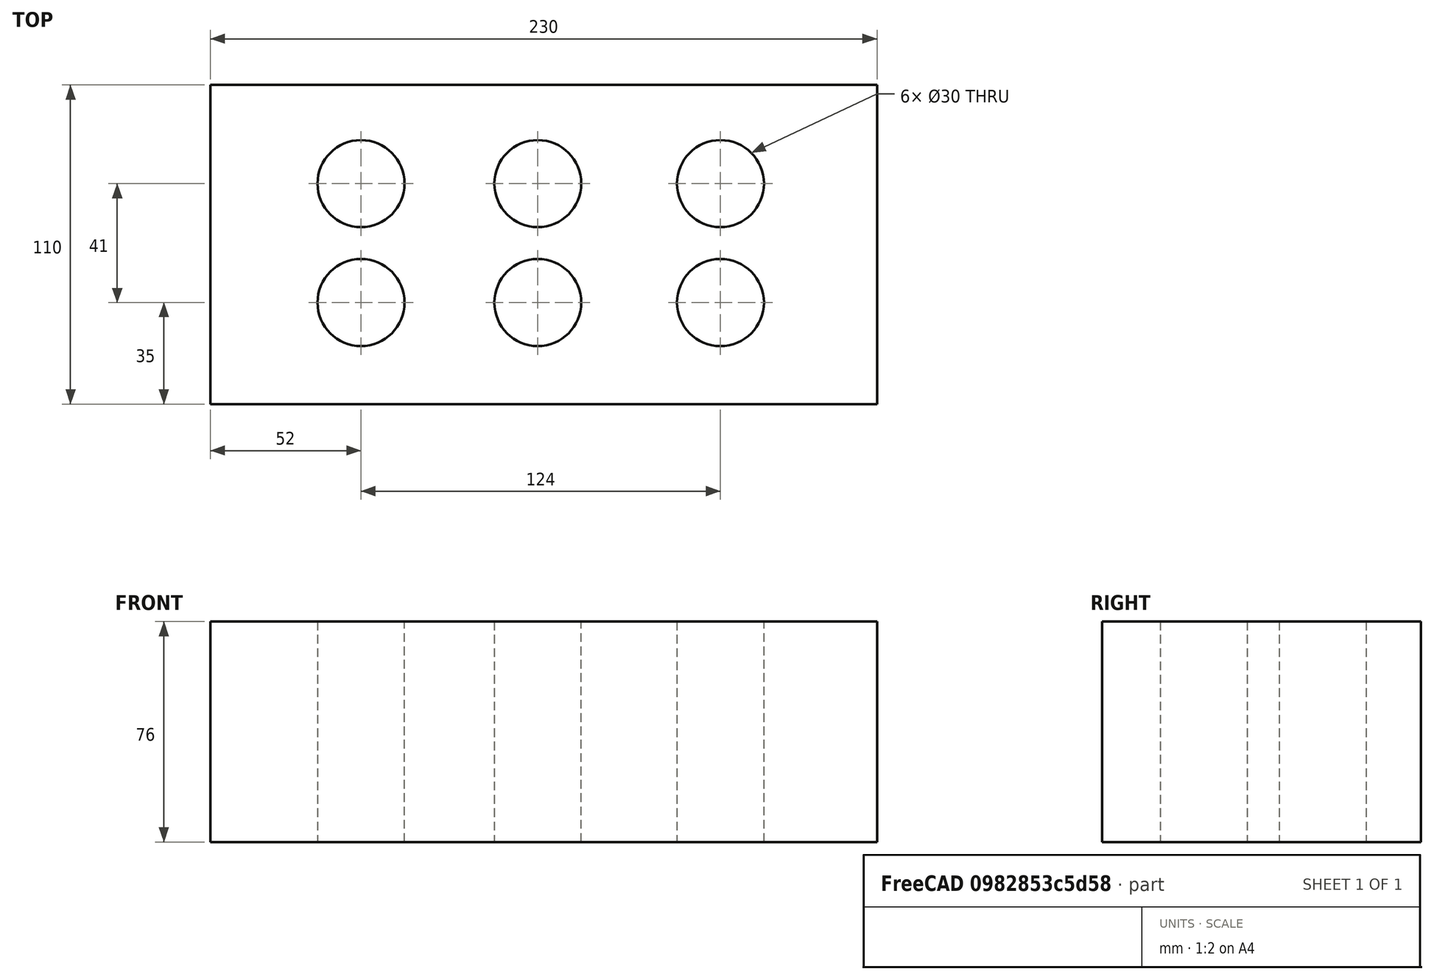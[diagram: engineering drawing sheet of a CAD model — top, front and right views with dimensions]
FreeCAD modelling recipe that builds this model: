
FCSTD DOCUMENT  (FreeCAD 1.0R39319 (Git))
Label: ojt1_t09r02_brik
License: All rights reserved
LicenseURL: https://en.wikipedia.org/wiki/All_rights_reserved
objects: Part::Cylinder×6, Part::Cut×6, Part::Box×1
note: 13 computed .brp shape members not serialized (recipe doc carries the construction recipe); baked Part::Feature solids carry a one-line shape summary decoded from their .brp

FEATURE [Part::Box] Box  label="Cub"
  AttacherType = Attacher::AttachEngine3D
  Height = 76
  Length = 230
  Width = 110
FEATURE [Part::Cylinder] Cylinder  label="Cilindre"
  Angle = 360
  AttacherType = Attacher::AttachEngine3D
  FirstAngle = 0
  Height = 82
  Placement = pos=(113,35,-4) rot=(0,0,1;0rad)
  Radius = 15
  SecondAngle = 0
FEATURE [Part::Cylinder] Cylinder001  label="Cilindre001"
  Angle = 360
  AttacherType = Attacher::AttachEngine3D
  FirstAngle = 0
  Height = 82
  Placement = pos=(176,76,-4) rot=(0,0,1;0rad)
  Radius = 15
  SecondAngle = 0
FEATURE [Part::Cylinder] Cylinder002  label="Cilindre002"
  Angle = 360
  AttacherType = Attacher::AttachEngine3D
  FirstAngle = 0
  Height = 82
  Placement = pos=(176,35,-4) rot=(0,0,1;0rad)
  Radius = 15
  SecondAngle = 0
FEATURE [Part::Cylinder] Cylinder003  label="Cilindre003"
  Angle = 360
  AttacherType = Attacher::AttachEngine3D
  FirstAngle = 0
  Height = 82
  Placement = pos=(113,76,-4) rot=(0,0,1;0rad)
  Radius = 15
  SecondAngle = 0
FEATURE [Part::Cylinder] Cylinder004  label="Cilindre004"
  Angle = 360
  AttacherType = Attacher::AttachEngine3D
  FirstAngle = 0
  Height = 82
  Placement = pos=(52,35,-4) rot=(0,0,1;0rad)
  Radius = 15
  SecondAngle = 0
FEATURE [Part::Cylinder] Cylinder005  label="Cilindre005"
  Angle = 360
  AttacherType = Attacher::AttachEngine3D
  FirstAngle = 0
  Height = 82
  Placement = pos=(52,76,-4) rot=(0,0,1;0rad)
  Radius = 15
  SecondAngle = 0
FEATURE [Part::Cut] Cut
  Base = -> Box
  Refine = true
  Tool = -> Cylinder
FEATURE [Part::Cut] Cut001
  Base = -> Cut
  Refine = true
  Tool = -> Cylinder005
FEATURE [Part::Cut] Cut002
  Base = -> Cut001
  Refine = true
  Tool = -> Cylinder004
FEATURE [Part::Cut] Cut003
  Base = -> Cut002
  Refine = true
  Tool = -> Cylinder003
FEATURE [Part::Cut] Cut004
  Base = -> Cut003
  Refine = true
  Tool = -> Cylinder002
FEATURE [Part::Cut] Cut005
  Base = -> Cut004
  Refine = true
  Tool = -> Cylinder001
